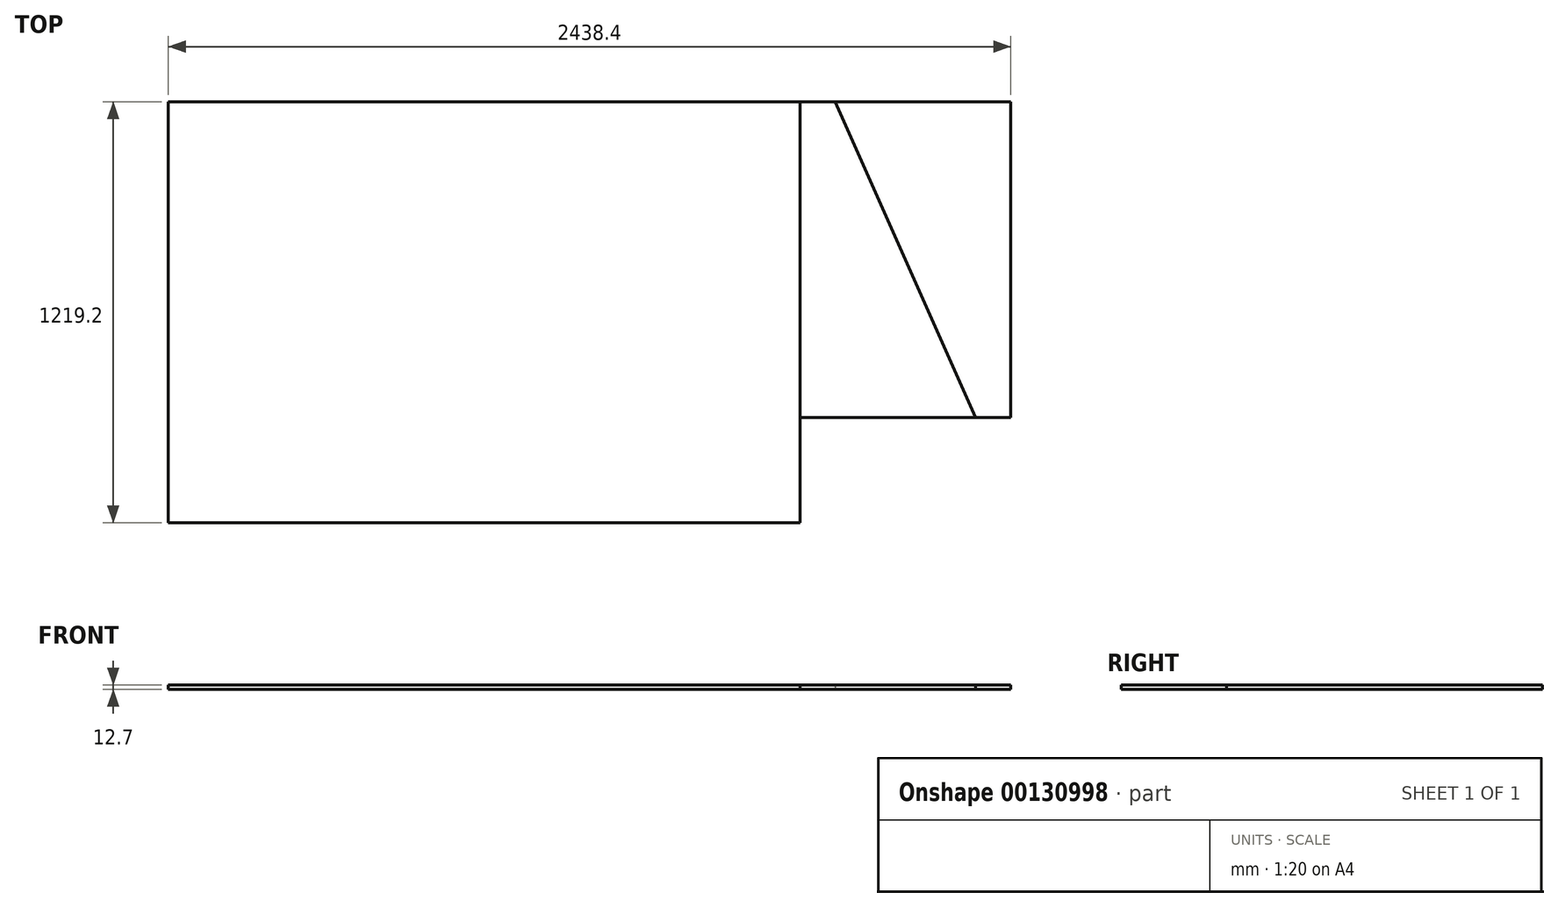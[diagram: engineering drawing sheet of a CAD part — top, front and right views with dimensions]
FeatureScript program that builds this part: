
annotation { "Feature Type Name" : "Feature", "Feature Type Description" : "" }
export const myFeature = defineFeature(function(context is Context, id is Id, definition is map)
    precondition{}
    {
        {
            var Q0;
            Q0=qCreatedBy(makeId("Top.planeOp"),FACE);
            var sketch = newSketch(context, id + "F0", { "sketchPlane" : qUnion([Q0])});
            skLineSegment(sketch, "E0.bottom", {"start": v(-1245.04, 550.6) * mm, "end": v(1193.36, 550.6) * mm});
            skLineSegment(sketch, "E0.top", {"start": v(-1245.04, -668.6) * mm, "end": v(1193.36, -668.6) * mm});
            skLineSegment(sketch, "E0.left", {"start": v(-1245.04, 550.6) * mm, "end": v(-1245.04, -668.6) * mm});
            skLineSegment(sketch, "E0.right", {"start": v(1193.36, 550.6) * mm, "end": v(1193.36, -668.6) * mm});
            skLineSegment(sketch, "E1", {"start": v(583.76, 550.6) * mm, "end": v(583.76, -668.6) * mm});
            skLineSegment(sketch, "E2", {"start": v(583.76, -363.8) * mm, "end": v(1193.36, -363.8) * mm});
            skLineSegment(sketch, "E3", {"start": v(685.36, 550.6) * mm, "end": v(1091.76, -363.8) * mm});
            skSolve(sketch);
        }
        {
            var Q0;
            {var subQ4=sQuery(id+"F0.wireOp",EDGE,"E0.left");Q0=makeQuery(id+"F0.imprint","IMPRINT",FACE,{"disambiguationData":[TD([[makeQuery(id+"F0.imprint","IMPRINT",EDGE,{"derivedFrom":subQ4}),1.0]])]});}
            extrude(context, id + "F1", {"entities" : qUnion([Q0]), "depth" : 12.7 * mm});
        }
        {
            var Q0;
            {var subQ3=sQuery(id+"F0.wireOp",EDGE,"E3");Q0=makeQuery(id+"F0.imprint","IMPRINT",FACE,{"disambiguationData":[TD([[makeQuery(id+"F0.imprint","IMPRINT",EDGE,{"derivedFrom":subQ3}),1.0]])]});}
            extrude(context, id + "F2", {"entities" : qUnion([Q0]), "depth" : 12.7 * mm});
        }
        {
            var Q0;
            {var subQ3=sQuery(id+"F0.wireOp",EDGE,"E3");Q0=makeQuery(id+"F0.imprint","IMPRINT",FACE,{"disambiguationData":[TD([[makeQuery(id+"F0.imprint","IMPRINT",EDGE,{"derivedFrom":subQ3}),-1.0]])]});}
            extrude(context, id + "F3", {"entities" : qUnion([Q0]), "depth" : 12.7 * mm});
        }
    });
